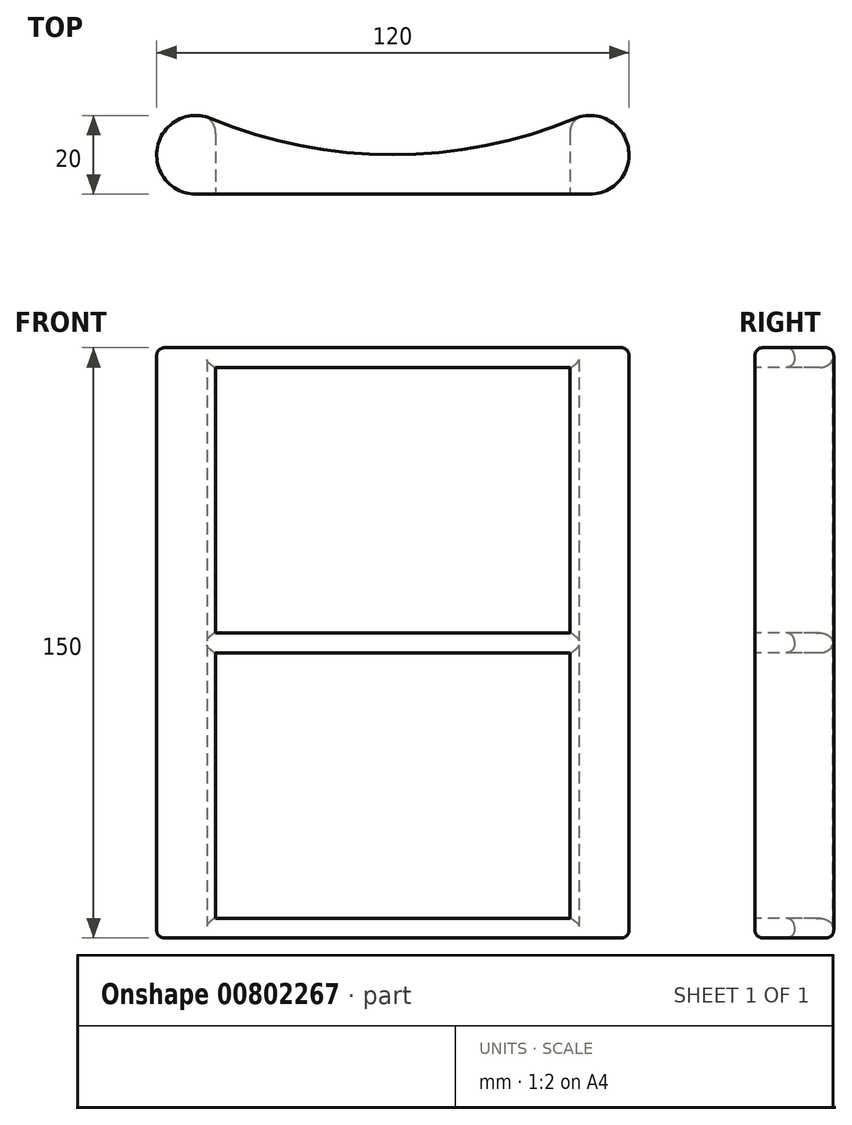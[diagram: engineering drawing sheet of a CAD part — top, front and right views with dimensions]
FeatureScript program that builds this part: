
annotation { "Feature Type Name" : "Feature", "Feature Type Description" : "" }
export const myFeature = defineFeature(function(context is Context, id is Id, definition is map)
    precondition{}
    {
        {
            var Q0;
            Q0=qCreatedBy(makeId("Top.planeOp"),FACE);
            var sketch = newSketch(context, id + "F0", { "sketchPlane" : qUnion([Q0])});
            skArc(sketch, "E0", {"start": v(-46.15, 9.23) * mm, "mid": v(-59.8, 1.96) * mm, "end": v(-50, -10) * mm});
            skArc(sketch, "E1", {"start": v(50, -10) * mm, "mid": v(59.8, 1.96) * mm, "end": v(46.15, 9.23) * mm});
            skLineSegment(sketch, "E2", {"start": v(-50, -10) * mm, "end": v(50, -10) * mm});
            skArc(sketch, "E3", {"start": v(-46.15, 9.23) * mm, "mid": v(0, 0) * mm, "end": v(46.15, 9.23) * mm});
            skSolve(sketch);
        }
        {
            var Q0;
            Q0=makeQuery(id+"F0.imprint","IMPRINT",FACE,{"disambiguationData":[TD([[makeQuery(id+"F0.imprint","IMPRINT",EDGE,{"derivedFrom":sQuery(id+"F0.wireOp",EDGE,"E0")}),1.0]])]});
            extrude(context, id + "F1", {"entities" : qUnion([Q0]), "depth" : 75 * mm, "offsetDistance" : 25 * mm, "hasSecondDirection" : true, "secondDirectionOppositeDirection" : true, "secondDirectionDepth" : 75 * mm});
        }
        {
            var Q0;
            Q0=makeQuery(id+"F1.opExtrude","SWEPT_FACE",FACE,{"disambiguationData":[OSD([sQuery(id+"F0.wireOp",EDGE,"E2")])]});
            var sketch = newSketch(context, id + "F2", { "sketchPlane" : qUnion([Q0])});
            skLineSegment(sketch, "E4.bottom", {"start": v(-45, -70) * mm, "end": v(45, -70) * mm});
            skLineSegment(sketch, "E4.top", {"start": v(-45, -2.5) * mm, "end": v(45, -2.5) * mm});
            skLineSegment(sketch, "E4.left", {"start": v(-45, -70) * mm, "end": v(-45, -2.5) * mm});
            skLineSegment(sketch, "E4.right", {"start": v(45, -70) * mm, "end": v(45, -2.5) * mm});
            skLineSegment(sketch, "E5.bottom", {"start": v(-45, 2.5) * mm, "end": v(45, 2.5) * mm});
            skLineSegment(sketch, "E5.top", {"start": v(-45, 70) * mm, "end": v(45, 70) * mm});
            skLineSegment(sketch, "E5.left", {"start": v(-45, 2.5) * mm, "end": v(-45, 70) * mm});
            skLineSegment(sketch, "E5.right", {"start": v(45, 2.5) * mm, "end": v(45, 70) * mm});
            skSolve(sketch);
        }
        {
            var Q0;
            Q0=makeQuery(id+"F2.imprint","IMPRINT",FACE,{"disambiguationData":[TD([[makeQuery(id+"F2.imprint","IMPRINT",EDGE,{"derivedFrom":sQuery(id+"F2.wireOp",EDGE,"E4.bottom")}),1.0]])]});
            var Q1;
            Q1=makeQuery(id+"F2.imprint","IMPRINT",FACE,{"disambiguationData":[TD([[makeQuery(id+"F2.imprint","IMPRINT",EDGE,{"derivedFrom":sQuery(id+"F2.wireOp",EDGE,"E5.bottom")}),1.0]])]});
            extrude(context, id + "F3", {"entities" : qUnion([Q0, Q1]), "operationType" : NewBodyOperationType.REMOVE, "oppositeDirection" : true, "depth" : 25 * mm, "offsetDistance" : 25 * mm});
        }
        {
            var Q0;
            Q0=makeQuery(id+"F3.boolean.opBoolean","INTERSECT",EDGE,{"derivedFrom":[makeQuery(id+"F1.opExtrude","SWEPT_FACE",FACE,{"disambiguationData":[OSD([sQuery(id+"F0.wireOp",EDGE,"E3")])]}),makeQuery(id+"F3.opExtrude","SWEPT_FACE",FACE,{"disambiguationData":[OSD([sQuery(id+"F2.wireOp",EDGE,"E5.left")])]})]});
            var Q1;
            Q1=makeQuery(id+"F3.boolean.opBoolean","INTERSECT",EDGE,{"derivedFrom":[makeQuery(id+"F1.opExtrude","SWEPT_FACE",FACE,{"disambiguationData":[OSD([sQuery(id+"F0.wireOp",EDGE,"E3")])]}),makeQuery(id+"F3.opExtrude","SWEPT_FACE",FACE,{"disambiguationData":[OSD([sQuery(id+"F2.wireOp",EDGE,"E4.left")])]})]});
            var Q2;
            Q2=makeQuery(id+"F1.opExtrude","SWEPT_EDGE",EDGE,{"disambiguationData":[OSD([sQuery(id+"F0.wireOp",EDGE,"E1"),sQuery(id+"F0.wireOp",EDGE,"E3")])]});
            var Q3;
            Q3=makeQuery(id+"F3.boolean.opBoolean","INTERSECT",EDGE,{"derivedFrom":[makeQuery(id+"F1.opExtrude","SWEPT_FACE",FACE,{"disambiguationData":[OSD([sQuery(id+"F0.wireOp",EDGE,"E3")])]}),makeQuery(id+"F3.opExtrude","SWEPT_FACE",FACE,{"disambiguationData":[OSD([sQuery(id+"F2.wireOp",EDGE,"E4.right")])]})]});
            var Q4;
            Q4=makeQuery(id+"F3.boolean.opBoolean","INTERSECT",EDGE,{"derivedFrom":[makeQuery(id+"F1.opExtrude","SWEPT_FACE",FACE,{"disambiguationData":[OSD([sQuery(id+"F0.wireOp",EDGE,"E3")])]}),makeQuery(id+"F3.opExtrude","SWEPT_FACE",FACE,{"disambiguationData":[OSD([sQuery(id+"F2.wireOp",EDGE,"E5.right")])]})]});
            fillet(context, id + "F4", {"entities" : qUnion([Q0, Q1, Q2, Q3, Q4]), "radius" : 5 * mm, "tangentPropagation" : true, "allowEdgeOverflow" : false});
        }
        {
            var Q0;
            Q0=makeQuery(id+"F1.opExtrude","CAP_FACE",FACE,{"disambiguationData":[OSD([sQuery(id+"F0.wireOp",EDGE,"E0"),sQuery(id+"F0.wireOp",EDGE,"E1"),sQuery(id+"F0.wireOp",EDGE,"E2"),sQuery(id+"F0.wireOp",EDGE,"E3")])],"isStart":true});
            var Q1;
            Q1=makeQuery(id+"F1.opExtrude","CAP_FACE",FACE,{"disambiguationData":[OSD([sQuery(id+"F0.wireOp",EDGE,"E0"),sQuery(id+"F0.wireOp",EDGE,"E1"),sQuery(id+"F0.wireOp",EDGE,"E2"),sQuery(id+"F0.wireOp",EDGE,"E3")])],"isStart":false});
            var Q2;
            Q2=makeQuery(id+"F4.opFillet","SPLIT",FACE,{"disambiguationData":[OD(2.0)],"derivedFrom":makeQuery(id+"F1.opExtrude","SWEPT_FACE",FACE,{"disambiguationData":[OSD([sQuery(id+"F0.wireOp",EDGE,"E3")])]})});
            var Q3;
            Q3=makeQuery(id+"F3.boolean.opBoolean","INTERSECT",EDGE,{"derivedFrom":[makeQuery(id+"F1.opExtrude","SWEPT_FACE",FACE,{"disambiguationData":[OSD([sQuery(id+"F0.wireOp",EDGE,"E3")])]}),makeQuery(id+"F3.opExtrude","SWEPT_FACE",FACE,{"disambiguationData":[OSD([sQuery(id+"F2.wireOp",EDGE,"E5.top")])]})]});
            var Q4;
            Q4=makeQuery(id+"F3.boolean.opBoolean","INTERSECT",EDGE,{"derivedFrom":[makeQuery(id+"F1.opExtrude","SWEPT_FACE",FACE,{"disambiguationData":[OSD([sQuery(id+"F0.wireOp",EDGE,"E3")])]}),makeQuery(id+"F3.opExtrude","SWEPT_FACE",FACE,{"disambiguationData":[OSD([sQuery(id+"F2.wireOp",EDGE,"E4.bottom")])]})]});
            fillet(context, id + "F5", {"entities" : qUnion([Q0, Q1, Q2, Q3, Q4]), "radius" : 2 * mm, "tangentPropagation" : true, "allowEdgeOverflow" : false});
        }
    });
